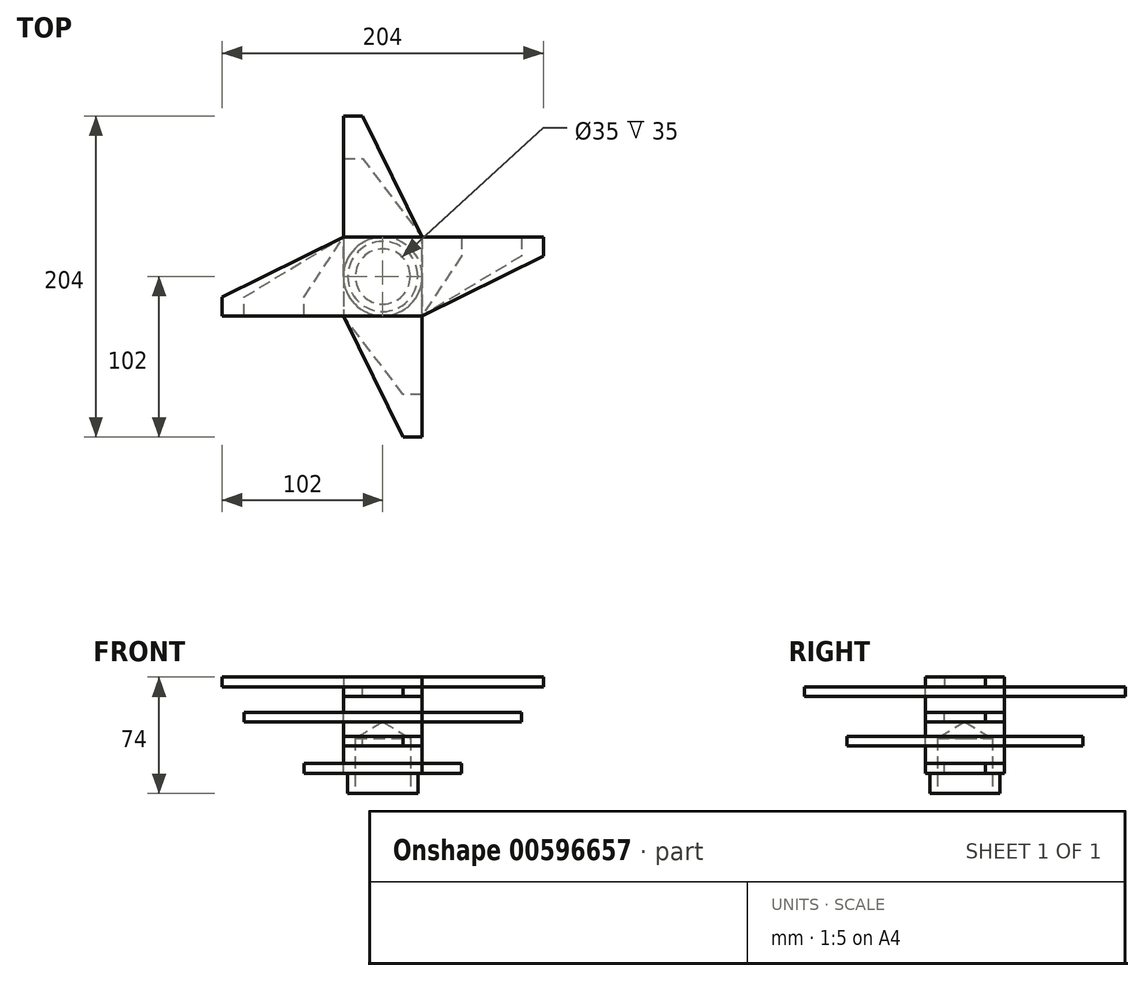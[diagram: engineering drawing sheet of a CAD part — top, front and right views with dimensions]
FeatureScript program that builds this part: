
annotation { "Feature Type Name" : "Feature", "Feature Type Description" : "" }
export const myFeature = defineFeature(function(context is Context, id is Id, definition is map)
    precondition{}
    {
        {
            var Q0;
            Q0=qCreatedBy(makeId("Top.planeOp"),FACE);
            var sketch = newSketch(context, id + "F0", { "sketchPlane" : qUnion([Q0])});
            skLineSegment(sketch, "E0.bottom", {"start": v(25, -25) * mm, "end": v(11.1, -25) * mm});
            skPoint(sketch, "E0.middle", {"position": v(0, 0) * mm});
            skLineSegment(sketch, "E1", {"start": v(102, 25) * mm, "end": v(102, 13) * mm});
            skLineSegment(sketch, "E2", {"start": v(102, 13) * mm, "end": v(25, -25) * mm});
            skLineSegment(sketch, "E3", {"start": v(-102, -25) * mm, "end": v(-102, -13) * mm});
            skLineSegment(sketch, "E4", {"start": v(-102, -13) * mm, "end": v(-25, 25) * mm});
            skLineSegment(sketch, "E5", {"start": v(-102, -25) * mm, "end": v(-11.1, -25) * mm});
            skLineSegment(sketch, "E6", {"start": v(11.1, -25) * mm, "end": v(25, -25) * mm});
            skLineSegment(sketch, "E7", {"start": v(-11.1, 25) * mm, "end": v(-25, 25) * mm});
            skPoint(sketch, "E8.orphan", {"position": v(-7.24, 25) * mm});
            skPoint(sketch, "E9.orphan", {"position": v(0, -25) * mm});
            skLineSegment(sketch, "E10", {"start": v(11.1, 25) * mm, "end": v(102, 25) * mm});
            skLineSegment(sketch, "E11", {"start": v(11.1, 25) * mm, "end": v(-11.1, 25) * mm});
            skLineSegment(sketch, "E12", {"start": v(-11.1, -25) * mm, "end": v(11.1, -25) * mm});
            skSolve(sketch);
        }
        {
            var Q0;
            Q0=makeQuery(id+"F0.imprint","IMPRINT",FACE,{"disambiguationData":[TD([[makeQuery(id+"F0.imprint","IMPRINT",EDGE,{"derivedFrom":sQuery(id+"F0.wireOp",EDGE,"hz4fnHxJ-RJTm-3U2X-LBAM-Hy0qQoeSoiVC")}),1.0]])]});
            var Q1;
            Q1=makeQuery(id+"F0.imprint","IMPRINT",FACE,{"disambiguationData":[TD([[makeQuery(id+"F0.imprint","IMPRINT",EDGE,{"derivedFrom":sQuery(id+"F0.wireOp",EDGE,"E1")}),-1.0]])]});
            extrude(context, id + "F1", {"entities" : qUnion([Q0, Q1]), "depth" : 6.2 * mm, "offsetDistance" : 25 * mm});
        }
        {
            var Q0;
            Q0=makeQuery(id+"F1.opExtrude","CAP_FACE",FACE,{"disambiguationData":[OSD([sQuery(id+"F0.wireOp",EDGE,"hz4fnHxJ-RJTm-3U2X-LBAM-Hy0qQoeSoiVC"),sQuery(id+"F0.wireOp",EDGE,"E1"),sQuery(id+"F0.wireOp",EDGE,"E2"),sQuery(id+"F0.wireOp",EDGE,"E3"),sQuery(id+"F0.wireOp",EDGE,"E4"),sQuery(id+"F0.wireOp",EDGE,"E5"),sQuery(id+"F0.wireOp",EDGE,"E6"),sQuery(id+"F0.wireOp",EDGE,"E7"),sQuery(id+"F0.wireOp",EDGE,"a48b50e9-9cfa-4d40-afe4-f468cfed9f28.trimOffspring"),sQuery(id+"F0.wireOp",EDGE,"E10")])],"isStart":true});
            var sketch = newSketch(context, id + "F2", { "sketchPlane" : qUnion([Q0])});
            skLineSegment(sketch, "E13", {"start": v(-25, 0) * mm, "end": v(-25, 25) * mm});
            skLineSegment(sketch, "E14", {"start": v(25, 102) * mm, "end": v(25, 0) * mm});
            skLineSegment(sketch, "E15", {"start": v(25, 0) * mm, "end": v(25, -25) * mm});
            skLineSegment(sketch, "E16", {"start": v(-25, -102) * mm, "end": v(-25, 0) * mm});
            skLineSegment(sketch, "E17", {"start": v(25, 102) * mm, "end": v(13, 102) * mm});
            skLineSegment(sketch, "E18", {"start": v(13, 102) * mm, "end": v(-25, 25) * mm});
            skLineSegment(sketch, "E19", {"start": v(-25, -102) * mm, "end": v(-13, -102) * mm});
            skLineSegment(sketch, "E20", {"start": v(-13, -102) * mm, "end": v(25, -25) * mm});
            skSolve(sketch);
        }
        {
            var Q0;
            {var subQ5=sQuery(id+"F2.wireOp",EDGE,"E13");Q0=makeQuery(id+"F2.imprint","IMPRINT",FACE,{"disambiguationData":[TD([[makeQuery(id+"F2.imprint","IMPRINT",EDGE,{"derivedFrom":subQ5}),-1.0]])]});}
            var Q1;
            {var subQ3=sQuery(id+"F2.wireOp",EDGE,"E19");Q1=makeQuery(id+"F2.imprint","IMPRINT",FACE,{"disambiguationData":[TD([[makeQuery(id+"F2.imprint","IMPRINT",EDGE,{"derivedFrom":subQ3}),1.0]])]});}
            var Q2;
            {var subQ2=sQuery(id+"F2.wireOp",EDGE,"E17");Q2=makeQuery(id+"F2.imprint","IMPRINT",FACE,{"disambiguationData":[TD([[makeQuery(id+"F2.imprint","IMPRINT",EDGE,{"derivedFrom":subQ2}),1.0]])]});}
            extrude(context, id + "F3", {"entities" : qUnion([Q0, Q1, Q2]), "operationType" : NewBodyOperationType.ADD, "depth" : 6.2 * mm, "offsetDistance" : 25 * mm});
        }
        {
            var Q0;
            Q0=makeQuery(id+"F3.opExtrude","CAP_FACE",FACE,{"disambiguationData":[OSD([sQuery(id+"F2.wireOp",EDGE,"E13"),sQuery(id+"F2.wireOp",EDGE,"E14"),sQuery(id+"F2.wireOp",EDGE,"E15"),sQuery(id+"F2.wireOp",EDGE,"E16"),sQuery(id+"F2.wireOp",EDGE,"E17"),sQuery(id+"F2.wireOp",EDGE,"E18"),sQuery(id+"F2.wireOp",EDGE,"E19"),sQuery(id+"F2.wireOp",EDGE,"E20")])],"isStart":false});
            var sketch = newSketch(context, id + "F4", { "sketchPlane" : qUnion([Q0])});
            skCircle(sketch, "E21", {"center": v(0, 0) * mm, "radius": 25 * mm});
            skSolve(sketch);
        }
        {
            var Q0;
            {var subQ0=sQuery(id+"F4.wireOp",EDGE,"E21");var subQ3=makeQuery(id+"F3.opExtrude","CAP_EDGE",EDGE,{"disambiguationData":[OSD([sQuery(id+"F2.wireOp",EDGE,"E20")])],"isStart":false});var subQ4=makeQuery(id+"F4.imprint","INTERSECT",VERTEX,{"derivedFrom":[subQ3,subQ0]});Q0=makeQuery(id+"F4.imprint","IMPRINT",FACE,{"disambiguationData":[TD([[makeQuery(id+"F4.imprint","IMPRINT",EDGE,{"disambiguationData":[TD([[subQ4,-1.0]])],"derivedFrom":subQ0}),1.0]])]});}
            var Q1;
            {var subQ3=sQuery(id+"F4.wireOp",EDGE,"E21");var subQ5=makeQuery(id+"F3.opExtrude","CAP_EDGE",EDGE,{"disambiguationData":[OSD([sQuery(id+"F2.wireOp",EDGE,"E18")])],"isStart":false});var subQ10=makeQuery(id+"F4.imprint","INTERSECT",VERTEX,{"derivedFrom":[subQ5,subQ3]});Q1=makeQuery(id+"F4.imprint","IMPRINT",FACE,{"disambiguationData":[TD([[makeQuery(id+"F4.imprint","IMPRINT",EDGE,{"disambiguationData":[TD([[subQ10,1.0]])],"derivedFrom":subQ3}),1.0]])]});}
            var Q2;
            {var subQ0=sQuery(id+"F4.wireOp",EDGE,"E21");var subQ1=makeQuery(id+"F3.opExtrude","CAP_EDGE",EDGE,{"disambiguationData":[OSD([sQuery(id+"F2.wireOp",EDGE,"E18")])],"isStart":false});var subQ2=makeQuery(id+"F4.imprint","INTERSECT",VERTEX,{"derivedFrom":[subQ1,subQ0]});Q2=makeQuery(id+"F4.imprint","IMPRINT",FACE,{"disambiguationData":[TD([[makeQuery(id+"F4.imprint","IMPRINT",EDGE,{"disambiguationData":[TD([[subQ2,-1.0]])],"derivedFrom":subQ0}),1.0]])]});}
            var Q3;
            {var subQ0=sQuery(id+"F4.wireOp",EDGE,"E21");var subQ1=makeQuery(id+"F3.opExtrude","CAP_EDGE",EDGE,{"disambiguationData":[OSD([sQuery(id+"F2.wireOp",EDGE,"E14"),sQuery(id+"F2.wireOp",EDGE,"E15")])],"isStart":false});var subQ2=makeQuery(id+"F4.imprint","INTERSECT",VERTEX,{"disambiguationData":[OD(0.0)],"derivedFrom":[subQ1,subQ0]});Q3=makeQuery(id+"F4.imprint","IMPRINT",FACE,{"disambiguationData":[TD([[makeQuery(id+"F4.imprint","IMPRINT",EDGE,{"disambiguationData":[TD([[subQ2,1.0]])],"derivedFrom":subQ0}),1.0]])]});}
            var Q4;
            {var subQ0=sQuery(id+"F4.wireOp",EDGE,"E21");var subQ1=makeQuery(id+"F3.opExtrude","CAP_EDGE",EDGE,{"disambiguationData":[OSD([sQuery(id+"F2.wireOp",EDGE,"E13"),sQuery(id+"F2.wireOp",EDGE,"E16")])],"isStart":false});var subQ2=makeQuery(id+"F4.imprint","INTERSECT",VERTEX,{"disambiguationData":[OD(0.0)],"derivedFrom":[subQ1,subQ0]});Q4=makeQuery(id+"F4.imprint","IMPRINT",FACE,{"disambiguationData":[TD([[makeQuery(id+"F4.imprint","IMPRINT",EDGE,{"disambiguationData":[TD([[subQ2,-1.0]])],"derivedFrom":subQ0}),1.0]])]});}
            extrude(context, id + "F5", {"entities" : qUnion([Q0, Q1, Q2, Q3, Q4]), "operationType" : NewBodyOperationType.ADD, "depth" : 10 * mm, "offsetDistance" : 25 * mm});
        }
        {
            var Q0;
            Q0=makeQuery(id+"F5.opExtrude","CAP_FACE",FACE,{"disambiguationData":[OSD([sQuery(id+"F4.wireOp",EDGE,"E21")])],"isStart":false});
            var sketch = newSketch(context, id + "F6", { "sketchPlane" : qUnion([Q0])});
            skLineSegment(sketch, "E22.bottom", {"start": v(25, -25) * mm, "end": v(-25, -25) * mm});
            skLineSegment(sketch, "E22.top", {"start": v(25, 25) * mm, "end": v(-25, 25) * mm});
            skLineSegment(sketch, "E22.left", {"start": v(25, -25) * mm, "end": v(25, 25) * mm});
            skLineSegment(sketch, "E22.right", {"start": v(-25, -25) * mm, "end": v(-25, 25) * mm});
            skPoint(sketch, "E22.middle", {"position": v(0, 0) * mm});
            skLineSegment(sketch, "E23", {"start": v(25, -25) * mm, "end": v(88, -25) * mm});
            skLineSegment(sketch, "E24", {"start": v(88, -25) * mm, "end": v(88, -13) * mm});
            skLineSegment(sketch, "E25", {"start": v(88, -13) * mm, "end": v(25, 25) * mm});
            skLineSegment(sketch, "E26", {"start": v(-25, 25) * mm, "end": v(-88, 25) * mm});
            skLineSegment(sketch, "E27", {"start": v(-88, 25) * mm, "end": v(-88, 13) * mm});
            skLineSegment(sketch, "E28", {"start": v(-88, 13) * mm, "end": v(-25, -25) * mm});
            skSolve(sketch);
        }
        {
            var Q0;
            Q0=makeQuery(id+"F6.imprint","IMPRINT",FACE,{"disambiguationData":[TD([[makeQuery(id+"F6.imprint","IMPRINT",EDGE,{"derivedFrom":sQuery(id+"F6.wireOp",EDGE,"E22.bottom")}),-1.0]])]});
            var Q1;
            Q1=makeQuery(id+"F6.imprint","IMPRINT",FACE,{"disambiguationData":[TD([[makeQuery(id+"F6.imprint","IMPRINT",EDGE,{"derivedFrom":sQuery(id+"F6.wireOp",EDGE,"E22.left")}),-1.0]])]});
            var Q2;
            Q2=makeQuery(id+"F6.imprint","IMPRINT",FACE,{"disambiguationData":[TD([[makeQuery(id+"F6.imprint","IMPRINT",EDGE,{"derivedFrom":sQuery(id+"F6.wireOp",EDGE,"E22.right")}),1.0]])]});
            var Q3;
            Q3=makeQuery(id+"F6.imprint","IMPRINT",FACE,{"disambiguationData":[TD([[makeQuery(id+"F6.imprint","IMPRINT",EDGE,{"derivedFrom":makeQuery(id+"F5.opExtrude","CAP_EDGE",EDGE,{"disambiguationData":[OSD([sQuery(id+"F4.wireOp",EDGE,"E21")])],"isStart":false})}),1.0]])]});
            var Q4;
            {var subQ1=sQuery(id+"F6.wireOp",EDGE,"E22.top");var subQ3=makeQuery(id+"F5.opExtrude","CAP_EDGE",EDGE,{"disambiguationData":[OSD([sQuery(id+"F4.wireOp",EDGE,"E21")])],"isStart":false});var subQ4=makeQuery(id+"F6.imprint","INTERSECT",VERTEX,{"derivedFrom":[subQ3,subQ1]});Q4=makeQuery(id+"F6.imprint","IMPRINT",FACE,{"disambiguationData":[TD([[makeQuery(id+"F6.imprint","IMPRINT",EDGE,{"disambiguationData":[TD([[subQ4,-1.0]])],"derivedFrom":subQ3}),-1.0]])]});}
            var Q5;
            {var subQ1=sQuery(id+"F6.wireOp",EDGE,"E22.top");var subQ3=makeQuery(id+"F5.opExtrude","CAP_EDGE",EDGE,{"disambiguationData":[OSD([sQuery(id+"F4.wireOp",EDGE,"E21")])],"isStart":false});var subQ4=makeQuery(id+"F6.imprint","INTERSECT",VERTEX,{"derivedFrom":[subQ3,subQ1]});Q5=makeQuery(id+"F6.imprint","IMPRINT",FACE,{"disambiguationData":[TD([[makeQuery(id+"F6.imprint","IMPRINT",EDGE,{"disambiguationData":[TD([[subQ4,1.0]])],"derivedFrom":subQ3}),-1.0]])]});}
            extrude(context, id + "F7", {"entities" : qUnion([Q0, Q1, Q2, Q3, Q4, Q5]), "operationType" : NewBodyOperationType.ADD, "depth" : 6.2 * mm, "offsetDistance" : 25 * mm});
        }
        {
            var Q0;
            Q0=makeQuery(id+"F7.opExtrude","CAP_FACE",FACE,{"disambiguationData":[OSD([sQuery(id+"F6.wireOp",EDGE,"E22.bottom"),sQuery(id+"F6.wireOp",EDGE,"E22.top"),sQuery(id+"F6.wireOp",EDGE,"E23"),sQuery(id+"F6.wireOp",EDGE,"E24"),sQuery(id+"F6.wireOp",EDGE,"E25"),sQuery(id+"F6.wireOp",EDGE,"E26"),sQuery(id+"F6.wireOp",EDGE,"E27"),sQuery(id+"F6.wireOp",EDGE,"E28")])],"isStart":false});
            var sketch = newSketch(context, id + "F8", { "sketchPlane" : qUnion([Q0])});
            skCircle(sketch, "E29", {"center": v(0, 0) * mm, "radius": 25 * mm});
            skSolve(sketch);
        }
        {
            var Q0;
            {var subQ0=sQuery(id+"F8.wireOp",EDGE,"E29");var subQ1=makeQuery(id+"F8.imprint","INTERSECT",VERTEX,{"derivedFrom":[makeQuery(id+"F7.opExtrude","CAP_EDGE",EDGE,{"disambiguationData":[OSD([sQuery(id+"F6.wireOp",EDGE,"E22.bottom"),sQuery(id+"F6.wireOp",EDGE,"E23")])],"isStart":false}),subQ0]});Q0=makeQuery(id+"F8.imprint","IMPRINT",FACE,{"disambiguationData":[TD([[makeQuery(id+"F8.imprint","IMPRINT",EDGE,{"disambiguationData":[TD([[subQ1,1.0]])],"derivedFrom":subQ0}),1.0]])]});}
            extrude(context, id + "F9", {"entities" : qUnion([Q0]), "operationType" : NewBodyOperationType.ADD, "depth" : 9 * mm, "offsetDistance" : 25 * mm});
        }
        {
            var Q0;
            Q0=makeQuery(id+"F9.opExtrude","CAP_FACE",FACE,{"disambiguationData":[OSD([sQuery(id+"F8.wireOp",EDGE,"E29")])],"isStart":false});
            var sketch = newSketch(context, id + "F10", { "sketchPlane" : qUnion([Q0])});
            skLineSegment(sketch, "E30.bottom", {"start": v(-25, -25) * mm, "end": v(25, -25) * mm});
            skLineSegment(sketch, "E30.top", {"start": v(-25, 25) * mm, "end": v(25, 25) * mm});
            skLineSegment(sketch, "E30.left", {"start": v(-25, -25) * mm, "end": v(-25, 25) * mm});
            skLineSegment(sketch, "E30.right", {"start": v(25, -25) * mm, "end": v(25, 25) * mm});
            skPoint(sketch, "E30.middle", {"position": v(0, 0) * mm});
            skLineSegment(sketch, "E31", {"start": v(25, 25) * mm, "end": v(25, 75) * mm});
            skLineSegment(sketch, "E32", {"start": v(25, 75) * mm, "end": v(13, 75) * mm});
            skLineSegment(sketch, "E33", {"start": v(13, 75) * mm, "end": v(-25, 25) * mm});
            skLineSegment(sketch, "E34", {"start": v(-25, -75) * mm, "end": v(-13, -75) * mm});
            skLineSegment(sketch, "E35", {"start": v(-13, -75) * mm, "end": v(25, -25) * mm});
            skLineSegment(sketch, "E36", {"start": v(-25, -25) * mm, "end": v(-25, -75) * mm});
            skSolve(sketch);
        }
        {
            var Q0;
            {var subQ0=sQuery(id+"F10.wireOp",EDGE,"E31");Q0=makeQuery(id+"F10.imprint","IMPRINT",FACE,{"disambiguationData":[TD([[makeQuery(id+"F10.imprint","IMPRINT",EDGE,{"derivedFrom":subQ0}),1.0]])]});}
            var Q1;
            {var subQ0=sQuery(id+"F10.wireOp",EDGE,"E30.right");var subQ3=makeQuery(id+"F9.opExtrude","CAP_EDGE",EDGE,{"disambiguationData":[OSD([sQuery(id+"F8.wireOp",EDGE,"E29")])],"isStart":false});var subQ5=makeQuery(id+"F10.imprint","INTERSECT",VERTEX,{"derivedFrom":[subQ3,subQ0]});Q1=makeQuery(id+"F10.imprint","IMPRINT",FACE,{"disambiguationData":[TD([[makeQuery(id+"F10.imprint","IMPRINT",EDGE,{"disambiguationData":[TD([[subQ5,-1.0]])],"derivedFrom":subQ3}),-1.0]])]});}
            var Q2;
            {var subQ0=makeQuery(id+"F9.opExtrude","CAP_EDGE",EDGE,{"disambiguationData":[OSD([sQuery(id+"F8.wireOp",EDGE,"E29")])],"isStart":false});var subQ1=makeQuery(id+"F10.imprint","INTERSECT",VERTEX,{"derivedFrom":[subQ0,sQuery(id+"F10.wireOp",EDGE,"E30.left")]});Q2=makeQuery(id+"F10.imprint","IMPRINT",FACE,{"disambiguationData":[TD([[makeQuery(id+"F10.imprint","IMPRINT",EDGE,{"disambiguationData":[TD([[subQ1,-1.0]])],"derivedFrom":subQ0}),1.0]])]});}
            var Q3;
            {var subQ0=sQuery(id+"F10.wireOp",EDGE,"E30.right");var subQ3=makeQuery(id+"F9.opExtrude","CAP_EDGE",EDGE,{"disambiguationData":[OSD([sQuery(id+"F8.wireOp",EDGE,"E29")])],"isStart":false});var subQ5=makeQuery(id+"F10.imprint","INTERSECT",VERTEX,{"derivedFrom":[subQ3,subQ0]});Q3=makeQuery(id+"F10.imprint","IMPRINT",FACE,{"disambiguationData":[TD([[makeQuery(id+"F10.imprint","IMPRINT",EDGE,{"disambiguationData":[TD([[subQ5,1.0]])],"derivedFrom":subQ3}),-1.0]])]});}
            var Q4;
            Q4=makeQuery(id+"F10.imprint","IMPRINT",FACE,{"disambiguationData":[TD([[makeQuery(id+"F10.imprint","IMPRINT",EDGE,{"derivedFrom":sQuery(id+"F10.wireOp",EDGE,"E34")}),1.0]])]});
            var Q5;
            {var subQ0=sQuery(id+"F10.wireOp",EDGE,"E30.left");var subQ3=makeQuery(id+"F9.opExtrude","CAP_EDGE",EDGE,{"disambiguationData":[OSD([sQuery(id+"F8.wireOp",EDGE,"E29")])],"isStart":false});var subQ5=makeQuery(id+"F10.imprint","INTERSECT",VERTEX,{"derivedFrom":[subQ3,subQ0]});Q5=makeQuery(id+"F10.imprint","IMPRINT",FACE,{"disambiguationData":[TD([[makeQuery(id+"F10.imprint","IMPRINT",EDGE,{"disambiguationData":[TD([[subQ5,-1.0]])],"derivedFrom":subQ3}),-1.0]])]});}
            var Q6;
            {var subQ0=sQuery(id+"F10.wireOp",EDGE,"E30.left");var subQ3=makeQuery(id+"F9.opExtrude","CAP_EDGE",EDGE,{"disambiguationData":[OSD([sQuery(id+"F8.wireOp",EDGE,"E29")])],"isStart":false});var subQ5=makeQuery(id+"F10.imprint","INTERSECT",VERTEX,{"derivedFrom":[subQ3,subQ0]});Q6=makeQuery(id+"F10.imprint","IMPRINT",FACE,{"disambiguationData":[TD([[makeQuery(id+"F10.imprint","IMPRINT",EDGE,{"disambiguationData":[TD([[subQ5,1.0]])],"derivedFrom":subQ3}),-1.0]])]});}
            extrude(context, id + "F11", {"entities" : qUnion([Q0, Q1, Q2, Q3, Q4, Q5, Q6]), "operationType" : NewBodyOperationType.ADD, "depth" : 6.2 * mm, "offsetDistance" : 25 * mm});
        }
        {
            var Q0;
            Q0=makeQuery(id+"F11.opExtrude","CAP_FACE",FACE,{"disambiguationData":[OSD([sQuery(id+"F10.wireOp",EDGE,"E30.left"),sQuery(id+"F10.wireOp",EDGE,"E30.right"),sQuery(id+"F10.wireOp",EDGE,"E31"),sQuery(id+"F10.wireOp",EDGE,"E32"),sQuery(id+"F10.wireOp",EDGE,"E33"),sQuery(id+"F10.wireOp",EDGE,"E34"),sQuery(id+"F10.wireOp",EDGE,"E35"),sQuery(id+"F10.wireOp",EDGE,"E36")])],"isStart":false});
            var sketch = newSketch(context, id + "F12", { "sketchPlane" : qUnion([Q0])});
            skCircle(sketch, "E37", {"center": v(0, 0) * mm, "radius": 25 * mm});
            skSolve(sketch);
        }
        {
            var Q0;
            {var subQ0=sQuery(id+"F12.wireOp",EDGE,"E37");var subQ1=makeQuery(id+"F12.imprint","INTERSECT",VERTEX,{"derivedFrom":[makeQuery(id+"F11.opExtrude","CAP_EDGE",EDGE,{"disambiguationData":[OSD([sQuery(id+"F10.wireOp",EDGE,"E30.left"),sQuery(id+"F10.wireOp",EDGE,"E36")])],"isStart":false}),subQ0]});Q0=makeQuery(id+"F12.imprint","IMPRINT",FACE,{"disambiguationData":[TD([[makeQuery(id+"F12.imprint","IMPRINT",EDGE,{"disambiguationData":[TD([[subQ1,1.0]])],"derivedFrom":subQ0}),1.0]])]});}
            extrude(context, id + "F13", {"entities" : qUnion([Q0]), "operationType" : NewBodyOperationType.ADD, "depth" : 11 * mm, "offsetDistance" : 25 * mm});
        }
        {
            var Q0;
            Q0=makeQuery(id+"F13.opExtrude","CAP_FACE",FACE,{"disambiguationData":[OSD([sQuery(id+"F12.wireOp",EDGE,"E37")])],"isStart":false});
            var sketch = newSketch(context, id + "F14", { "sketchPlane" : qUnion([Q0])});
            skLineSegment(sketch, "E38.bottom", {"start": v(25, -25) * mm, "end": v(-25, -25) * mm});
            skLineSegment(sketch, "E38.top", {"start": v(25, 25) * mm, "end": v(-25, 25) * mm});
            skLineSegment(sketch, "E38.left", {"start": v(25, -25) * mm, "end": v(25, 25) * mm});
            skLineSegment(sketch, "E38.right", {"start": v(-25, -25) * mm, "end": v(-25, 25) * mm});
            skPoint(sketch, "E38.middle", {"position": v(0, 0) * mm});
            skLineSegment(sketch, "E39", {"start": v(25, -25) * mm, "end": v(50, -25) * mm});
            skLineSegment(sketch, "E40", {"start": v(50, -25) * mm, "end": v(50, -13) * mm});
            skLineSegment(sketch, "E41", {"start": v(50, -13) * mm, "end": v(25, 25) * mm});
            skLineSegment(sketch, "E42", {"start": v(-25, 25) * mm, "end": v(-50, 25) * mm});
            skLineSegment(sketch, "E43", {"start": v(-50, 25) * mm, "end": v(-50, 13) * mm});
            skLineSegment(sketch, "E44", {"start": v(-50, 13) * mm, "end": v(-25, -25) * mm});
            skSolve(sketch);
        }
        {
            var Q0;
            {var subQ0=makeQuery(id+"F13.opExtrude","CAP_EDGE",EDGE,{"disambiguationData":[OSD([sQuery(id+"F12.wireOp",EDGE,"E37")])],"isStart":false});var subQ1=makeQuery(id+"F14.imprint","INTERSECT",VERTEX,{"derivedFrom":[subQ0,sQuery(id+"F14.wireOp",EDGE,"E38.bottom")]});Q0=makeQuery(id+"F14.imprint","IMPRINT",FACE,{"disambiguationData":[TD([[makeQuery(id+"F14.imprint","IMPRINT",EDGE,{"disambiguationData":[TD([[subQ1,-1.0]])],"derivedFrom":subQ0}),1.0]])]});}
            var Q1;
            {var subQ1=sQuery(id+"F14.wireOp",EDGE,"E38.top");var subQ3=makeQuery(id+"F13.opExtrude","CAP_EDGE",EDGE,{"disambiguationData":[OSD([sQuery(id+"F12.wireOp",EDGE,"E37")])],"isStart":false});var subQ4=makeQuery(id+"F14.imprint","INTERSECT",VERTEX,{"derivedFrom":[subQ3,subQ1]});Q1=makeQuery(id+"F14.imprint","IMPRINT",FACE,{"disambiguationData":[TD([[makeQuery(id+"F14.imprint","IMPRINT",EDGE,{"disambiguationData":[TD([[subQ4,1.0]])],"derivedFrom":subQ3}),-1.0]])]});}
            var Q2;
            {var subQ1=sQuery(id+"F14.wireOp",EDGE,"E38.bottom");var subQ3=makeQuery(id+"F13.opExtrude","CAP_EDGE",EDGE,{"disambiguationData":[OSD([sQuery(id+"F12.wireOp",EDGE,"E37")])],"isStart":false});var subQ4=makeQuery(id+"F14.imprint","INTERSECT",VERTEX,{"derivedFrom":[subQ3,subQ1]});Q2=makeQuery(id+"F14.imprint","IMPRINT",FACE,{"disambiguationData":[TD([[makeQuery(id+"F14.imprint","IMPRINT",EDGE,{"disambiguationData":[TD([[subQ4,-1.0]])],"derivedFrom":subQ3}),-1.0]])]});}
            var Q3;
            {var subQ1=sQuery(id+"F14.wireOp",EDGE,"E38.bottom");var subQ3=makeQuery(id+"F13.opExtrude","CAP_EDGE",EDGE,{"disambiguationData":[OSD([sQuery(id+"F12.wireOp",EDGE,"E37")])],"isStart":false});var subQ4=makeQuery(id+"F14.imprint","INTERSECT",VERTEX,{"derivedFrom":[subQ3,subQ1]});Q3=makeQuery(id+"F14.imprint","IMPRINT",FACE,{"disambiguationData":[TD([[makeQuery(id+"F14.imprint","IMPRINT",EDGE,{"disambiguationData":[TD([[subQ4,1.0]])],"derivedFrom":subQ3}),-1.0]])]});}
            var Q4;
            {var subQ1=sQuery(id+"F14.wireOp",EDGE,"E38.top");var subQ3=makeQuery(id+"F13.opExtrude","CAP_EDGE",EDGE,{"disambiguationData":[OSD([sQuery(id+"F12.wireOp",EDGE,"E37")])],"isStart":false});var subQ4=makeQuery(id+"F14.imprint","INTERSECT",VERTEX,{"derivedFrom":[subQ3,subQ1]});Q4=makeQuery(id+"F14.imprint","IMPRINT",FACE,{"disambiguationData":[TD([[makeQuery(id+"F14.imprint","IMPRINT",EDGE,{"disambiguationData":[TD([[subQ4,-1.0]])],"derivedFrom":subQ3}),-1.0]])]});}
            var Q5;
            {var subQ0=sQuery(id+"F14.wireOp",EDGE,"E42");Q5=makeQuery(id+"F14.imprint","IMPRINT",FACE,{"disambiguationData":[TD([[makeQuery(id+"F14.imprint","IMPRINT",EDGE,{"derivedFrom":subQ0}),1.0]])]});}
            var Q6;
            {var subQ0=sQuery(id+"F14.wireOp",EDGE,"E39");Q6=makeQuery(id+"F14.imprint","IMPRINT",FACE,{"disambiguationData":[TD([[makeQuery(id+"F14.imprint","IMPRINT",EDGE,{"derivedFrom":subQ0}),1.0]])]});}
            extrude(context, id + "F15", {"entities" : qUnion([Q0, Q1, Q2, Q3, Q4, Q5, Q6]), "operationType" : NewBodyOperationType.ADD, "depth" : 6.2 * mm, "offsetDistance" : 25 * mm});
        }
        {
            var Q0;
            Q0=makeQuery(id+"F15.opExtrude","CAP_FACE",FACE,{"disambiguationData":[OSD([sQuery(id+"F14.wireOp",EDGE,"E38.bottom"),sQuery(id+"F14.wireOp",EDGE,"E38.top"),sQuery(id+"F14.wireOp",EDGE,"E39"),sQuery(id+"F14.wireOp",EDGE,"E40"),sQuery(id+"F14.wireOp",EDGE,"E41"),sQuery(id+"F14.wireOp",EDGE,"E42"),sQuery(id+"F14.wireOp",EDGE,"E43"),sQuery(id+"F14.wireOp",EDGE,"E44")])],"isStart":false});
            var sketch = newSketch(context, id + "F16", { "sketchPlane" : qUnion([Q0])});
            skCircle(sketch, "E45", {"center": v(0, 0) * mm, "radius": 22.25 * mm});
            skSolve(sketch);
        }
        {
            var Q0;
            Q0=makeQuery(id+"F16.imprint","IMPRINT",FACE,{"disambiguationData":[TD([[makeQuery(id+"F16.imprint","IMPRINT",EDGE,{"derivedFrom":sQuery(id+"F16.wireOp",EDGE,"E45")}),1.0]])]});
            extrude(context, id + "F17", {"entities" : qUnion([Q0]), "operationType" : NewBodyOperationType.ADD, "depth" : 13 * mm, "offsetDistance" : 25 * mm});
        }
        {
            var Q0;
            Q0=makeQuery(id+"F17.opExtrude","CAP_FACE",FACE,{"disambiguationData":[OSD([sQuery(id+"F16.wireOp",EDGE,"E45")])],"isStart":false});
            var sketch = newSketch(context, id + "F18", { "sketchPlane" : qUnion([Q0])});
            skPoint(sketch, "E46", {"position": v(0, 0) * mm});
            skSolve(sketch);
        }
        {
            var Q0;
            Q0=sQuery(id+"F18.wireOp",VERTEX,"E46");
            var Q1;
            Q1=makeQuery(id+"F1.opExtrude","SWEPT_BODY",BODY,{"disambiguationData":[OSD([sQuery(id+"F0.wireOp",EDGE,"hz4fnHxJ-RJTm-3U2X-LBAM-Hy0qQoeSoiVC"),sQuery(id+"F0.wireOp",EDGE,"E1"),sQuery(id+"F0.wireOp",EDGE,"E2"),sQuery(id+"F0.wireOp",EDGE,"E3"),sQuery(id+"F0.wireOp",EDGE,"E4"),sQuery(id+"F0.wireOp",EDGE,"E5"),sQuery(id+"F0.wireOp",EDGE,"E6"),sQuery(id+"F0.wireOp",EDGE,"E7"),sQuery(id+"F0.wireOp",EDGE,"a48b50e9-9cfa-4d40-afe4-f468cfed9f28.trimOffspring"),sQuery(id+"F0.wireOp",EDGE,"E10")])]});
            hole(context, id + "F19", {"style" : HoleStyle.SIMPLE, "endStyle" : HoleEndStyle.BLIND, "holeDiameter" : 35 * mm, "majorDiameter" : 5 * mm, "holeDepth" : 35 * mm, "isTappedThrough" : true, "tappedDepth" : 12 * mm, "tapClearance" : 3, "startFromSketch" : true, "locations" : qUnion([Q0]), "scope" : qUnion([Q1])});
        }
    });
